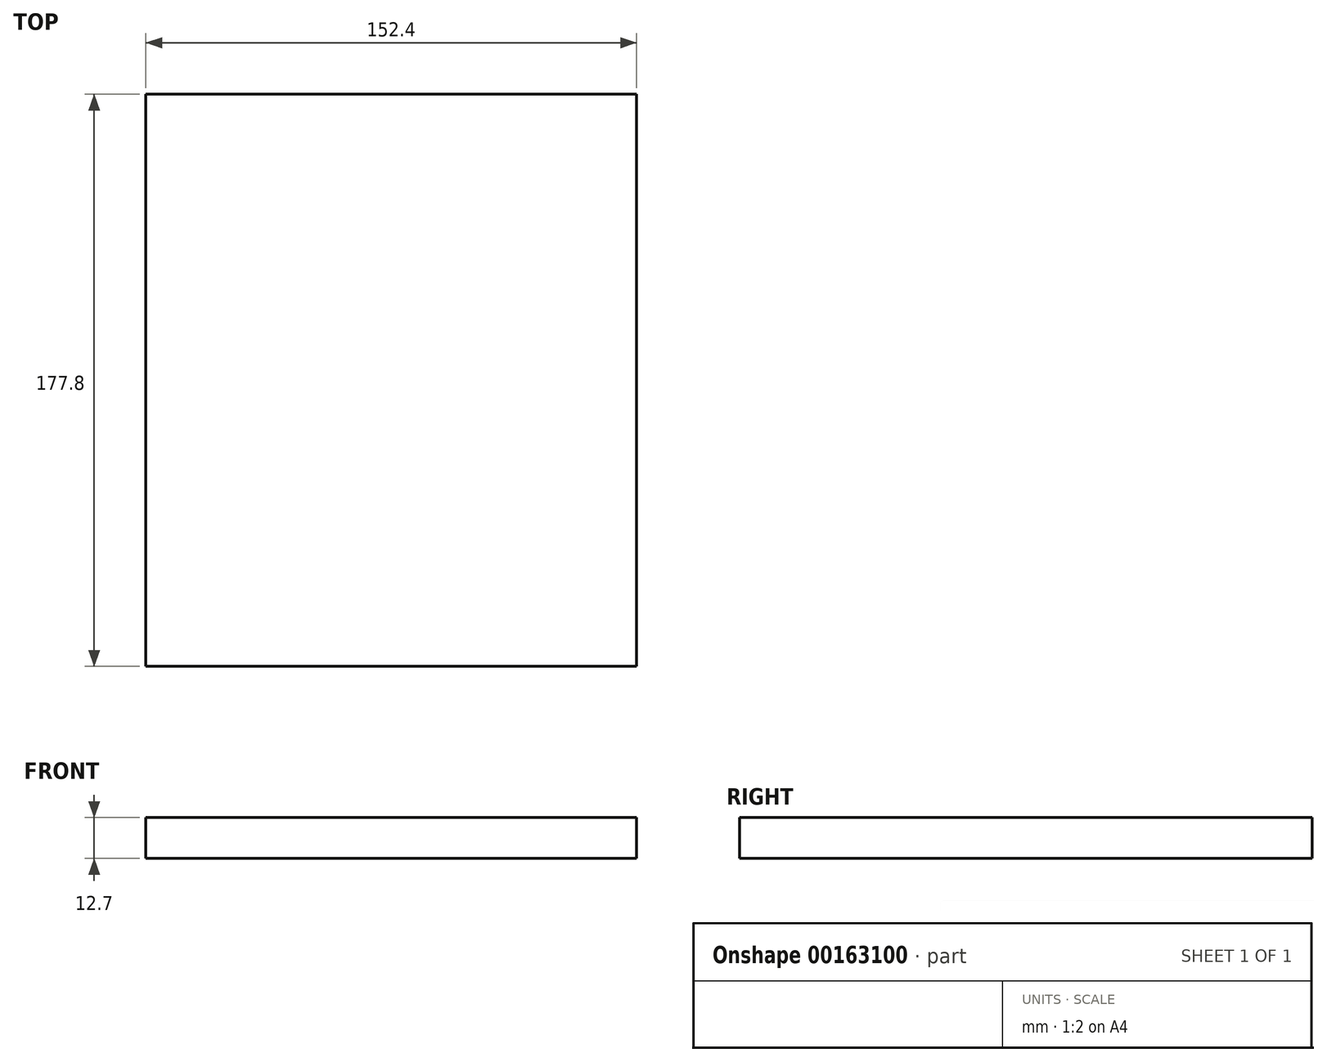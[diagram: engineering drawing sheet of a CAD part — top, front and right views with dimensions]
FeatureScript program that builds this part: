
annotation { "Feature Type Name" : "Feature", "Feature Type Description" : "" }
export const myFeature = defineFeature(function(context is Context, id is Id, definition is map)
    precondition{}
    {
        {
            var Q0;
            Q0=qCreatedBy(makeId("Top.planeOp"),FACE);
            var sketch = newSketch(context, id + "F0", { "sketchPlane" : qUnion([Q0])});
            skLineSegment(sketch, "E0.bottom", {"start": v(-76.03, 74.92) * mm, "end": v(76.37, 74.92) * mm});
            skLineSegment(sketch, "E0.top", {"start": v(-76.03, -102.88) * mm, "end": v(76.37, -102.88) * mm});
            skLineSegment(sketch, "E0.left", {"start": v(-76.03, 74.92) * mm, "end": v(-76.03, -102.88) * mm});
            skLineSegment(sketch, "E0.right", {"start": v(76.37, 74.92) * mm, "end": v(76.37, -102.88) * mm});
            skSolve(sketch);
        }
        {
            var Q0;
            Q0=makeQuery(id+"F0.imprint","IMPRINT",FACE,{"disambiguationData":[TD([[makeQuery(id+"F0.imprint","IMPRINT",EDGE,{"derivedFrom":sQuery(id+"F0.wireOp",EDGE,"E0.bottom")}),-1.0]])]});
            extrude(context, id + "F1", {"entities" : qUnion([Q0]), "depth" : 12.7 * mm});
        }
    });
